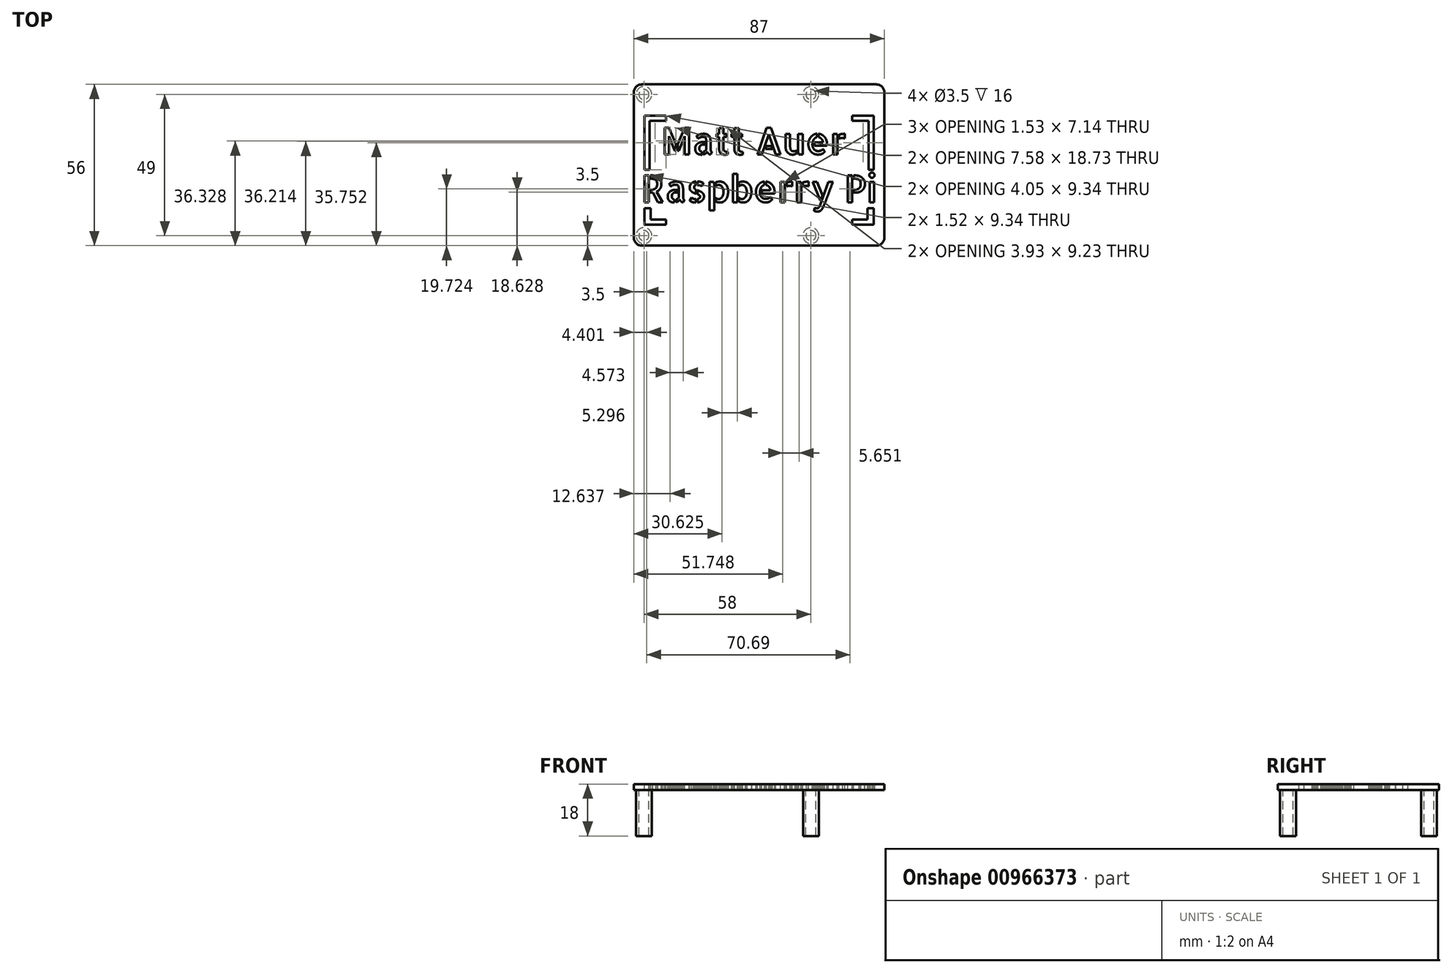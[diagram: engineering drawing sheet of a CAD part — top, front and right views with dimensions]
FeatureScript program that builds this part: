
annotation { "Feature Type Name" : "Feature", "Feature Type Description" : "" }
export const myFeature = defineFeature(function(context is Context, id is Id, definition is map)
    precondition{}
    {
        {
            var Q0;
            Q0=qCreatedBy(makeId("Top.planeOp"),FACE);
            var sketch = newSketch(context, id + "F0", { "sketchPlane" : qUnion([Q0])});
            skLineSegment(sketch, "E0.bottom", {"start": v(2.8, 0) * mm, "end": v(84.2, 0) * mm});
            skLineSegment(sketch, "E0.top", {"start": v(2.8, 56) * mm, "end": v(84.2, 56) * mm});
            skLineSegment(sketch, "E0.left", {"start": v(0, 2.8) * mm, "end": v(0, 53.2) * mm});
            skLineSegment(sketch, "E0.right", {"start": v(87, 2.8) * mm, "end": v(87, 53.2) * mm});
            skCircle(sketch, "E1", {"center": v(3.5, 3.5) * mm, "radius": 1.15 * mm});
            skCircle(sketch, "E2", {"center": v(3.5, 52.5) * mm, "radius": 1.15 * mm});
            skCircle(sketch, "E3", {"center": v(61.5, 52.5) * mm, "radius": 1.15 * mm});
            skCircle(sketch, "E4", {"center": v(61.5, 3.5) * mm, "radius": 1.15 * mm});
            skPoint(sketch, "E5.visualSharp", {"position": v(0, 0) * mm});
            skArc(sketch, "E5.filletArc", {"start": v(0, 2.8) * mm, "mid": v(0.82, 0.82) * mm, "end": v(2.8, 0) * mm});
            skPoint(sketch, "E6.visualSharp", {"position": v(87, 0) * mm});
            skArc(sketch, "E6.filletArc", {"start": v(84.2, 0) * mm, "mid": v(86.18, 0.82) * mm, "end": v(87, 2.8) * mm});
            skPoint(sketch, "E7.visualSharp", {"position": v(87, 56) * mm});
            skArc(sketch, "E7.filletArc", {"start": v(87, 53.2) * mm, "mid": v(86.18, 55.18) * mm, "end": v(84.2, 56) * mm});
            skPoint(sketch, "E8.visualSharp", {"position": v(0, 56) * mm});
            skArc(sketch, "E8.filletArc", {"start": v(2.8, 56) * mm, "mid": v(0.82, 55.18) * mm, "end": v(0, 53.2) * mm});
            skSolve(sketch);
        }
        {
            var Q0;
            Q0=makeQuery(id+"F0.imprint","IMPRINT",FACE,{"disambiguationData":[TD([[makeQuery(id+"F0.imprint","IMPRINT",EDGE,{"derivedFrom":sQuery(id+"F0.wireOp",EDGE,"E0.bottom")}),1.0]])]});
            var Q1;
            Q1=makeQuery(id+"F0.imprint","IMPRINT",FACE,{"disambiguationData":[TD([[makeQuery(id+"F0.imprint","IMPRINT",EDGE,{"derivedFrom":sQuery(id+"F0.wireOp",EDGE,"E1")}),1.0]])]});
            var Q2;
            Q2=makeQuery(id+"F0.imprint","IMPRINT",FACE,{"disambiguationData":[TD([[makeQuery(id+"F0.imprint","IMPRINT",EDGE,{"derivedFrom":sQuery(id+"F0.wireOp",EDGE,"E3")}),1.0]])]});
            var Q3;
            Q3=makeQuery(id+"F0.imprint","IMPRINT",FACE,{"disambiguationData":[TD([[makeQuery(id+"F0.imprint","IMPRINT",EDGE,{"derivedFrom":sQuery(id+"F0.wireOp",EDGE,"E4")}),1.0]])]});
            var Q4;
            Q4=makeQuery(id+"F0.imprint","IMPRINT",FACE,{"disambiguationData":[TD([[makeQuery(id+"F0.imprint","IMPRINT",EDGE,{"derivedFrom":sQuery(id+"F0.wireOp",EDGE,"E3")}),1.0]])]});
            var Q5;
            Q5=makeQuery(id+"F0.imprint","IMPRINT",FACE,{"disambiguationData":[TD([[makeQuery(id+"F0.imprint","IMPRINT",EDGE,{"derivedFrom":sQuery(id+"F0.wireOp",EDGE,"E4")}),1.0]])]});
            var Q6;
            Q6=makeQuery(id+"F0.imprint","IMPRINT",FACE,{"disambiguationData":[TD([[makeQuery(id+"F0.imprint","IMPRINT",EDGE,{"derivedFrom":sQuery(id+"F0.wireOp",EDGE,"E2")}),1.0]])]});
            extrude(context, id + "F1", {"entities" : qUnion([Q0, Q1, Q2, Q3, Q4, Q5, Q6]), "depth" : 2 * mm, "offsetDistance" : 25 * mm});
        }
        {
            var Q0;
            Q0=makeQuery(id+"F0.imprint","IMPRINT",FACE,{"disambiguationData":[TD([[makeQuery(id+"F0.imprint","IMPRINT",EDGE,{"derivedFrom":sQuery(id+"F0.wireOp",EDGE,"E4")}),1.0]])]});
            var Q1;
            Q1=makeQuery(id+"F0.imprint","IMPRINT",FACE,{"disambiguationData":[TD([[makeQuery(id+"F0.imprint","IMPRINT",EDGE,{"derivedFrom":sQuery(id+"F0.wireOp",EDGE,"E3")}),1.0]])]});
            var Q2;
            Q2=makeQuery(id+"F0.imprint","IMPRINT",FACE,{"disambiguationData":[TD([[makeQuery(id+"F0.imprint","IMPRINT",EDGE,{"derivedFrom":sQuery(id+"F0.wireOp",EDGE,"E2")}),1.0]])]});
            var Q3;
            Q3=makeQuery(id+"F0.imprint","IMPRINT",FACE,{"disambiguationData":[TD([[makeQuery(id+"F0.imprint","IMPRINT",EDGE,{"derivedFrom":sQuery(id+"F0.wireOp",EDGE,"E1")}),1.0]])]});
            extrude(context, id + "F2", {"entities" : qUnion([Q0, Q1, Q2, Q3]), "operationType" : NewBodyOperationType.ADD, "depth" : 105 * mm, "offsetDistance" : 25 * mm});
        }
        {
            var Q0;
            Q0=qCreatedBy(makeId("Top.planeOp"),FACE);
            cPlane(context, id + "F3", {"entities" : qUnion([Q0]), "cplaneType" : CPlaneType.OFFSET, "offset" : 25 * mm, "width" : 150 * mm, "height" : 150 * mm});
        }
        {
            var Q0;
            Q0=qCreatedBy(id+"F3.planeOp",FACE);
            var sketch = newSketch(context, id + "F4", { "sketchPlane" : qUnion([Q0])});
            skPoint(sketch, "E9.0", {"position": v(3.5, 52.5) * mm});
            skPoint(sketch, "E10.0", {"position": v(61.5, 52.5) * mm});
            skPoint(sketch, "E11.0", {"position": v(3.5, 3.5) * mm});
            skPoint(sketch, "E12.0", {"position": v(61.5, 3.5) * mm});
            skLineSegment(sketch, "E13.0", {"start": v(2.8, 56) * mm, "end": v(84.2, 56) * mm});
            skPoint(sketch, "E14.0", {"position": v(0.82, 55.18) * mm});
            skLineSegment(sketch, "E15.0", {"start": v(0, 2.8) * mm, "end": v(0, 53.2) * mm});
            skArc(sketch, "E16.0", {"start": v(2.8, 56) * mm, "mid": v(0.82, 55.18) * mm, "end": v(0, 53.2) * mm});
            skArc(sketch, "E17.0", {"start": v(87, 53.2) * mm, "mid": v(86.18, 55.18) * mm, "end": v(84.2, 56) * mm});
            skLineSegment(sketch, "E18.0", {"start": v(87, 2.8) * mm, "end": v(87, 53.2) * mm});
            skLineSegment(sketch, "E19.0", {"start": v(2.8, 0) * mm, "end": v(84.2, 0) * mm});
            skArc(sketch, "E20.0", {"start": v(84.2, 0) * mm, "mid": v(86.18, 0.82) * mm, "end": v(87, 2.8) * mm});
            skArc(sketch, "E21.0", {"start": v(0, 2.8) * mm, "mid": v(0.82, 0.82) * mm, "end": v(2.8, 0) * mm});
            skCircle(sketch, "E22", {"center": v(3.5, 52.5) * mm, "radius": 1.75 * mm});
            skCircle(sketch, "E23", {"center": v(3.5, 3.5) * mm, "radius": 1.75 * mm});
            skCircle(sketch, "E24", {"center": v(61.5, 3.5) * mm, "radius": 1.75 * mm});
            skCircle(sketch, "E25", {"center": v(61.5, 52.5) * mm, "radius": 1.75 * mm});
            skCircle(sketch, "E26", {"center": v(3.5, 3.5) * mm, "radius": 2.75 * mm});
            skCircle(sketch, "E27", {"center": v(61.5, 3.5) * mm, "radius": 2.75 * mm});
            skCircle(sketch, "E28", {"center": v(3.5, 52.5) * mm, "radius": 2.75 * mm});
            skCircle(sketch, "E29", {"center": v(61.5, 52.5) * mm, "radius": 2.75 * mm});
            skSolve(sketch);
        }
        {
            var Q0;
            Q0=makeQuery(id+"F4.imprint","IMPRINT",FACE,{"disambiguationData":[TD([[makeQuery(id+"F4.imprint","IMPRINT",EDGE,{"derivedFrom":sQuery(id+"F4.wireOp",EDGE,"E23")}),1.0]])]});
            var Q1;
            Q1=makeQuery(id+"F4.imprint","IMPRINT",FACE,{"disambiguationData":[TD([[makeQuery(id+"F4.imprint","IMPRINT",EDGE,{"derivedFrom":sQuery(id+"F4.wireOp",EDGE,"E23")}),-1.0]])]});
            var Q2;
            Q2=makeQuery(id+"F4.imprint","IMPRINT",FACE,{"disambiguationData":[TD([[makeQuery(id+"F4.imprint","IMPRINT",EDGE,{"derivedFrom":sQuery(id+"F4.wireOp",EDGE,"E13.0")}),-1.0]])]});
            var Q3;
            Q3=makeQuery(id+"F4.imprint","IMPRINT",FACE,{"disambiguationData":[TD([[makeQuery(id+"F4.imprint","IMPRINT",EDGE,{"derivedFrom":sQuery(id+"F4.wireOp",EDGE,"E24")}),-1.0]])]});
            var Q4;
            Q4=makeQuery(id+"F4.imprint","IMPRINT",FACE,{"disambiguationData":[TD([[makeQuery(id+"F4.imprint","IMPRINT",EDGE,{"derivedFrom":sQuery(id+"F4.wireOp",EDGE,"E24")}),1.0]])]});
            var Q5;
            Q5=makeQuery(id+"F4.imprint","IMPRINT",FACE,{"disambiguationData":[TD([[makeQuery(id+"F4.imprint","IMPRINT",EDGE,{"derivedFrom":sQuery(id+"F4.wireOp",EDGE,"E25")}),-1.0]])]});
            var Q6;
            Q6=makeQuery(id+"F4.imprint","IMPRINT",FACE,{"disambiguationData":[TD([[makeQuery(id+"F4.imprint","IMPRINT",EDGE,{"derivedFrom":sQuery(id+"F4.wireOp",EDGE,"E25")}),1.0]])]});
            var Q7;
            Q7=makeQuery(id+"F4.imprint","IMPRINT",FACE,{"disambiguationData":[TD([[makeQuery(id+"F4.imprint","IMPRINT",EDGE,{"derivedFrom":sQuery(id+"F4.wireOp",EDGE,"E22")}),-1.0]])]});
            var Q8;
            Q8=makeQuery(id+"F4.imprint","IMPRINT",FACE,{"disambiguationData":[TD([[makeQuery(id+"F4.imprint","IMPRINT",EDGE,{"derivedFrom":sQuery(id+"F4.wireOp",EDGE,"E22")}),1.0]])]});
            extrude(context, id + "F5", {"entities" : qUnion([Q0, Q1, Q2, Q3, Q4, Q5, Q6, Q7, Q8]), "depth" : 2 * mm, "offsetDistance" : 25 * mm});
        }
        {
            var Q0;
            Q0=makeQuery(id+"F4.imprint","IMPRINT",FACE,{"disambiguationData":[TD([[makeQuery(id+"F4.imprint","IMPRINT",EDGE,{"derivedFrom":sQuery(id+"F4.wireOp",EDGE,"E23")}),-1.0]])]});
            var Q1;
            Q1=makeQuery(id+"F4.imprint","IMPRINT",FACE,{"disambiguationData":[TD([[makeQuery(id+"F4.imprint","IMPRINT",EDGE,{"derivedFrom":sQuery(id+"F4.wireOp",EDGE,"E22")}),-1.0]])]});
            var Q2;
            Q2=makeQuery(id+"F4.imprint","IMPRINT",FACE,{"disambiguationData":[TD([[makeQuery(id+"F4.imprint","IMPRINT",EDGE,{"derivedFrom":sQuery(id+"F4.wireOp",EDGE,"E25")}),-1.0]])]});
            var Q3;
            Q3=makeQuery(id+"F4.imprint","IMPRINT",FACE,{"disambiguationData":[TD([[makeQuery(id+"F4.imprint","IMPRINT",EDGE,{"derivedFrom":sQuery(id+"F4.wireOp",EDGE,"E24")}),-1.0]])]});
            var Q4;
            Q4=makeQuery(id+"F5.opExtrude","CAP_FACE",FACE,{"disambiguationData":[OSD([sQuery(id+"F4.wireOp",EDGE,"E13.0"),sQuery(id+"F4.wireOp",EDGE,"E15.0"),sQuery(id+"F4.wireOp",EDGE,"E16.0"),sQuery(id+"F4.wireOp",EDGE,"E17.0"),sQuery(id+"F4.wireOp",EDGE,"E18.0"),sQuery(id+"F4.wireOp",EDGE,"E19.0"),sQuery(id+"F4.wireOp",EDGE,"E20.0"),sQuery(id+"F4.wireOp",EDGE,"E21.0"),sQuery(id+"F4.wireOp",EDGE,"E26"),sQuery(id+"F4.wireOp",EDGE,"E27"),sQuery(id+"F4.wireOp",EDGE,"E28"),sQuery(id+"F4.wireOp",EDGE,"E29")])],"isStart":false});
            var Q5;
            Q5=makeQuery(id+"F5.opExtrude","SWEPT_BODY",BODY,{"disambiguationData":[OSD([sQuery(id+"F4.wireOp",EDGE,"E13.0"),sQuery(id+"F4.wireOp",EDGE,"E15.0"),sQuery(id+"F4.wireOp",EDGE,"E16.0"),sQuery(id+"F4.wireOp",EDGE,"E17.0"),sQuery(id+"F4.wireOp",EDGE,"E18.0"),sQuery(id+"F4.wireOp",EDGE,"E19.0"),sQuery(id+"F4.wireOp",EDGE,"E20.0"),sQuery(id+"F4.wireOp",EDGE,"E21.0"),sQuery(id+"F4.wireOp",EDGE,"E26"),sQuery(id+"F4.wireOp",EDGE,"E27"),sQuery(id+"F4.wireOp",EDGE,"E28"),sQuery(id+"F4.wireOp",EDGE,"E29")])]});
            extrude(context, id + "F6", {"entities" : qUnion([Q0, Q1, Q2, Q3]), "operationType" : NewBodyOperationType.ADD, "endBound" : BoundingType.UP_TO_SURFACE, "depth" : 20 * mm, "endBoundEntityFace" : qUnion([Q4]), "endBoundEntityBody" : qUnion([Q5]), "offsetDistance" : 25 * mm});
        }
        {
            var Q0;
            Q0=makeQuery(id+"F4.imprint","IMPRINT",FACE,{"disambiguationData":[TD([[makeQuery(id+"F4.imprint","IMPRINT",EDGE,{"derivedFrom":sQuery(id+"F4.wireOp",EDGE,"E23")}),-1.0]])]});
            var Q1;
            Q1=makeQuery(id+"F4.imprint","IMPRINT",FACE,{"disambiguationData":[TD([[makeQuery(id+"F4.imprint","IMPRINT",EDGE,{"derivedFrom":sQuery(id+"F4.wireOp",EDGE,"E22")}),-1.0]])]});
            var Q2;
            Q2=makeQuery(id+"F4.imprint","IMPRINT",FACE,{"disambiguationData":[TD([[makeQuery(id+"F4.imprint","IMPRINT",EDGE,{"derivedFrom":sQuery(id+"F4.wireOp",EDGE,"E24")}),-1.0]])]});
            var Q3;
            Q3=makeQuery(id+"F4.imprint","IMPRINT",FACE,{"disambiguationData":[TD([[makeQuery(id+"F4.imprint","IMPRINT",EDGE,{"derivedFrom":sQuery(id+"F4.wireOp",EDGE,"E25")}),-1.0]])]});
            extrude(context, id + "F7", {"entities" : qUnion([Q0, Q1, Q2, Q3]), "operationType" : NewBodyOperationType.ADD, "oppositeDirection" : true, "depth" : 16 * mm, "offsetDistance" : 25 * mm});
        }
        {
            var Q0;
            Q0=makeQuery(id+"F1.opExtrude","SWEPT_BODY",BODY,{"disambiguationData":[OSD([sQuery(id+"F0.wireOp",EDGE,"E0.bottom"),sQuery(id+"F0.wireOp",EDGE,"E0.top"),sQuery(id+"F0.wireOp",EDGE,"E0.left"),sQuery(id+"F0.wireOp",EDGE,"E0.right"),sQuery(id+"F0.wireOp",EDGE,"E5.filletArc"),sQuery(id+"F0.wireOp",EDGE,"E6.filletArc"),sQuery(id+"F0.wireOp",EDGE,"E7.filletArc"),sQuery(id+"F0.wireOp",EDGE,"E8.filletArc")])]});
            deleteBodies(context, id + "F8", {"entities" : qUnion([Q0])});
        }
        {
            var Q0;
            Q0=makeQuery(id+"F5.opExtrude","CAP_FACE",FACE,{"disambiguationData":[OSD([sQuery(id+"F4.wireOp",EDGE,"E13.0"),sQuery(id+"F4.wireOp",EDGE,"E15.0"),sQuery(id+"F4.wireOp",EDGE,"E16.0"),sQuery(id+"F4.wireOp",EDGE,"E17.0"),sQuery(id+"F4.wireOp",EDGE,"E18.0"),sQuery(id+"F4.wireOp",EDGE,"E19.0"),sQuery(id+"F4.wireOp",EDGE,"E20.0"),sQuery(id+"F4.wireOp",EDGE,"E21.0")])],"isStart":false});
            var sketch = newSketch(context, id + "F9", { "sketchPlane" : qUnion([Q0])});
            skCircle(sketch, "E30.0", {"center": v(3.5, 52.5) * mm, "radius": 1.15 * mm});
            skCircle(sketch, "E31.0", {"center": v(61.5, 52.5) * mm, "radius": 1.15 * mm});
            skCircle(sketch, "E32.0", {"center": v(61.5, 3.5) * mm, "radius": 1.15 * mm});
            skCircle(sketch, "E33.0", {"center": v(3.5, 3.5) * mm, "radius": 1.15 * mm});
            skSolve(sketch);
        }
        {
            var Q0;
            Q0=makeQuery(id+"F9.imprint","IMPRINT",FACE,{"disambiguationData":[TD([[makeQuery(id+"F9.imprint","IMPRINT",EDGE,{"derivedFrom":sQuery(id+"F9.wireOp",EDGE,"E30.0")}),-1.0]])]});
            var sketch = newSketch(context, id + "F10", { "sketchPlane" : qUnion([Q0])});
            skText(sketch, "E34", { "text": "  Matt Auer\nRaspberry Pi", "fontName": "AllertaStencil-Regular.ttf"});
            const initialGuessF10  = {"E34": [0.0025, 0.03166, 1, 0, 0.00934]};
            skSetInitialGuess(sketch, initialGuessF10);
            skSolve(sketch);
        }
        {
            var Q0;
            Q0 = qSketchRegion(id + "F10", true);
            extrude(context, id + "F11", {"entities" : qUnion([Q0]), "operationType" : NewBodyOperationType.REMOVE, "oppositeDirection" : true, "depth" : 2 * mm, "offsetDistance" : 25 * mm});
        }
        {
            var Q0;
            Q0=makeQuery(id+"F9.imprint","IMPRINT",FACE,{"disambiguationData":[TD([[makeQuery(id+"F9.imprint","IMPRINT",EDGE,{"derivedFrom":sQuery(id+"F9.wireOp",EDGE,"E30.0")}),-1.0]])]});
            var sketch = newSketch(context, id + "F12", { "sketchPlane" : qUnion([Q0])});
            skLineSegment(sketch, "E35", {"start": v(11.22, 45.12) * mm, "end": v(3.64, 45.12) * mm});
            skLineSegment(sketch, "E36", {"start": v(3.64, 45.12) * mm, "end": v(3.64, 26.39) * mm});
            skLineSegment(sketch, "E37", {"start": v(3.64, 26.39) * mm, "end": v(5.42, 26.39) * mm});
            skLineSegment(sketch, "E38", {"start": v(5.42, 26.39) * mm, "end": v(5.42, 43.34) * mm});
            skLineSegment(sketch, "E39", {"start": v(5.42, 43.34) * mm, "end": v(11.22, 43.34) * mm});
            skLineSegment(sketch, "E40", {"start": v(11.22, 43.34) * mm, "end": v(11.22, 45.12) * mm});
            skLineSegment(sketch, "E41", {"start": v(3.64, 13.05) * mm, "end": v(3.64, 7.32) * mm});
            skLineSegment(sketch, "E42", {"start": v(3.64, 7.32) * mm, "end": v(11.22, 7.32) * mm});
            skLineSegment(sketch, "E43", {"start": v(11.22, 7.32) * mm, "end": v(11.22, 9.1) * mm});
            skLineSegment(sketch, "E44", {"start": v(11.22, 9.1) * mm, "end": v(5.81, 9.1) * mm});
            skLineSegment(sketch, "E45", {"start": v(5.81, 9.1) * mm, "end": v(5.81, 13.05) * mm});
            skLineSegment(sketch, "E46", {"start": v(5.81, 13.05) * mm, "end": v(3.64, 13.05) * mm});
            skPoint(sketch, "E47.0", {"position": v(43.5, 56) * mm});
            skPoint(sketch, "E48.0", {"position": v(43.5, 0) * mm});
            skLineSegment(sketch, "E49", {"start": v(43.5, 56) * mm, "end": v(43.5, 0) * mm, "construction": true});
            skLineSegment(sketch, "E50.MirrorCS", {"start": v(81.58, 43.34) * mm, "end": v(75.78, 43.34) * mm});
            skLineSegment(sketch, "E51.MirrorCS", {"start": v(75.78, 45.12) * mm, "end": v(83.36, 45.12) * mm});
            skLineSegment(sketch, "E52.MirrorCS", {"start": v(81.58, 26.39) * mm, "end": v(81.58, 43.34) * mm});
            skLineSegment(sketch, "E53.MirrorCS", {"start": v(83.36, 45.12) * mm, "end": v(83.36, 26.39) * mm});
            skLineSegment(sketch, "E54.MirrorCS", {"start": v(75.78, 7.32) * mm, "end": v(75.78, 9.1) * mm});
            skLineSegment(sketch, "E55.MirrorCS", {"start": v(83.36, 13.05) * mm, "end": v(83.36, 7.32) * mm});
            skLineSegment(sketch, "E56.MirrorCS", {"start": v(81.19, 9.1) * mm, "end": v(81.19, 13.05) * mm});
            skLineSegment(sketch, "E57.MirrorCS", {"start": v(75.78, 9.1) * mm, "end": v(81.19, 9.1) * mm});
            skLineSegment(sketch, "E58.MirrorCS", {"start": v(83.36, 7.32) * mm, "end": v(75.78, 7.32) * mm});
            skLineSegment(sketch, "E59.MirrorCS", {"start": v(83.36, 26.39) * mm, "end": v(81.58, 26.39) * mm});
            skLineSegment(sketch, "E60.MirrorCS", {"start": v(81.19, 13.05) * mm, "end": v(83.36, 13.05) * mm});
            skLineSegment(sketch, "E61.MirrorCS", {"start": v(75.78, 43.34) * mm, "end": v(75.78, 45.12) * mm});
            skSolve(sketch);
        }
        {
            var Q0;
            Q0 = qSketchRegion(id + "F12", true);
            extrude(context, id + "F13", {"entities" : qUnion([Q0]), "operationType" : NewBodyOperationType.REMOVE, "oppositeDirection" : true, "depth" : 2 * mm, "offsetDistance" : 25 * mm});
        }
    });
